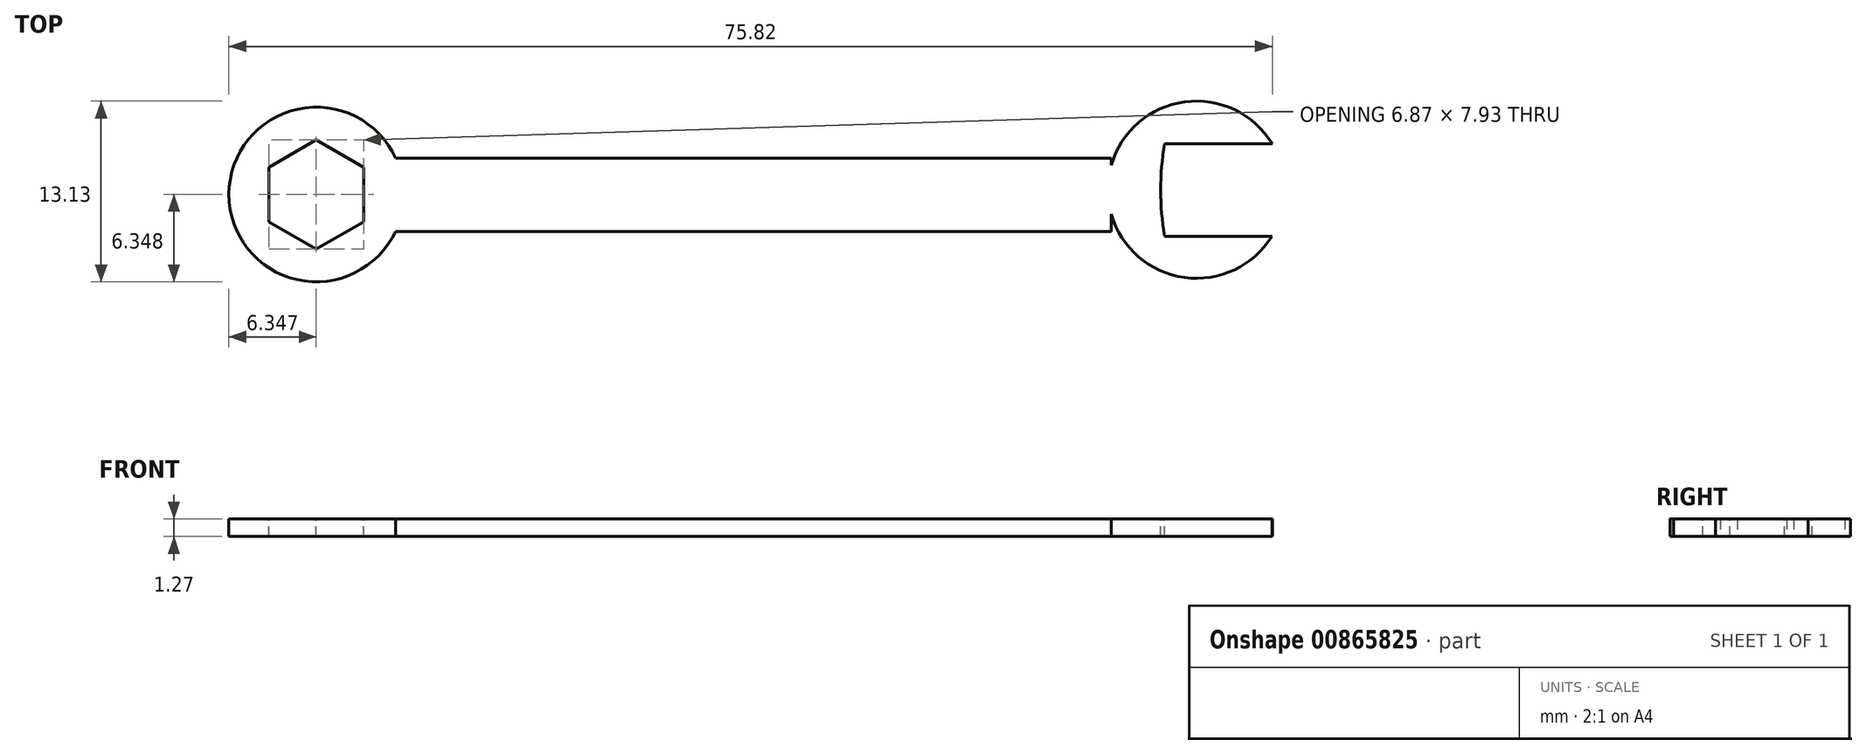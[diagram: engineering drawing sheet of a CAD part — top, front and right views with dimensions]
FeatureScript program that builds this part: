
annotation { "Feature Type Name" : "Feature", "Feature Type Description" : "" }
export const myFeature = defineFeature(function(context is Context, id is Id, definition is map)
    precondition{}
    {
        {
            var Q0;
            Q0=qCreatedBy(makeId("Top.planeOp"),FACE);
            var sketch = newSketch(context, id + "F0", { "sketchPlane" : qUnion([Q0])});
            skCircle(sketch, "E0", {"center": v(-57.77, 15.17) * mm, "radius": 6.35 * mm});
            skSolve(sketch);
        }
        {
            var Q0;
            Q0=makeQuery(id+"F0.imprint","IMPRINT",FACE,{"disambiguationData":[TD([[makeQuery(id+"F0.imprint","IMPRINT",EDGE,{"derivedFrom":sQuery(id+"F0.wireOp",EDGE,"E0")}),1.0]])]});
            extrude(context, id + "F1", {"entities" : qUnion([Q0]), "depth" : 1.27 * mm, "offsetDistance" : 25.4 * mm});
        }
        {
            var Q0;
            Q0=makeQuery(id+"F0.imprint","IMPRINT",FACE,{"disambiguationData":[TD([[makeQuery(id+"F0.imprint","IMPRINT",EDGE,{"derivedFrom":sQuery(id+"F0.wireOp",EDGE,"E0")}),1.0]])]});
            extrude(context, id + "F2", {"entities" : qUnion([Q0]), "operationType" : NewBodyOperationType.ADD, "depth" : 1.27 * mm, "offsetDistance" : 25.4 * mm});
        }
        {
            var Q0;
            Q0=qCreatedBy(makeId("Top.planeOp"),FACE);
            var sketch = newSketch(context, id + "F3", { "sketchPlane" : qUnion([Q0])});
            skLineSegment(sketch, "E1.bottom", {"start": v(-52.79, 12.49) * mm, "end": v(0, 12.49) * mm});
            skLineSegment(sketch, "E1.top", {"start": v(-52.79, 17.8) * mm, "end": v(0, 17.8) * mm});
            skLineSegment(sketch, "E1.left", {"start": v(-52.79, 12.49) * mm, "end": v(-52.79, 17.8) * mm});
            skLineSegment(sketch, "E1.right", {"start": v(0, 12.49) * mm, "end": v(0, 17.8) * mm});
            skSolve(sketch);
        }
        {
            var Q0;
            Q0 = qSketchRegion(id + "F3", true);
            extrude(context, id + "F4", {"entities" : qUnion([Q0]), "operationType" : NewBodyOperationType.ADD, "depth" : 1.27 * mm, "offsetDistance" : 25.4 * mm});
        }
        {
            var Q0;
            Q0=qCreatedBy(makeId("Top.planeOp"),FACE);
            var sketch = newSketch(context, id + "F5", { "sketchPlane" : qUnion([Q0])});
            skCircle(sketch, "E2", {"center": v(6.2, 15.51) * mm, "radius": 6.44 * mm});
            skSolve(sketch);
        }
        {
            var Q0;
            Q0 = qSketchRegion(id + "F5", true);
            extrude(context, id + "F6", {"entities" : qUnion([Q0]), "operationType" : NewBodyOperationType.ADD, "depth" : 1.27 * mm, "offsetDistance" : 25.4 * mm});
        }
        {
            var Q0;
            Q0=makeQuery(id+"F6.boolean.opBoolean","MERGE",FACE,{"derivedFrom":[makeQuery(id+"F4.boolean.opBoolean","MERGE",FACE,{"derivedFrom":[makeQuery(id+"F1.opExtrude","CAP_FACE",FACE,{"disambiguationData":[OSD([sQuery(id+"F0.wireOp",EDGE,"E0")])],"isStart":false}),makeQuery(id+"F4.opExtrude","CAP_FACE",FACE,{"disambiguationData":[OSD([sQuery(id+"F3.wireOp",EDGE,"E1.bottom"),sQuery(id+"F3.wireOp",EDGE,"E1.top"),sQuery(id+"F3.wireOp",EDGE,"E1.left"),sQuery(id+"F3.wireOp",EDGE,"E1.right")])],"isStart":false})]}),makeQuery(id+"F6.opExtrude","CAP_FACE",FACE,{"disambiguationData":[OSD([sQuery(id+"F5.wireOp",EDGE,"E2")])],"isStart":false})]});
            var sketch = newSketch(context, id + "F7", { "sketchPlane" : qUnion([Q0])});
            skCircle(sketch, "E3.cCircle", {"center": v(-57.77, 15.17) * mm, "radius": 3.43 * mm, "construction": true});
            skLineSegment(sketch, "E3.0", {"start": v(-54.34, 17.15) * mm, "end": v(-54.34, 13.19) * mm});
            skLineSegment(sketch, "E3.1", {"start": v(-54.34, 13.19) * mm, "end": v(-57.77, 11.2) * mm});
            skLineSegment(sketch, "E3.2", {"start": v(-57.77, 11.2) * mm, "end": v(-61.2, 13.19) * mm});
            skLineSegment(sketch, "E3.3", {"start": v(-61.2, 13.19) * mm, "end": v(-61.2, 17.15) * mm});
            skLineSegment(sketch, "E3.4", {"start": v(-61.2, 17.15) * mm, "end": v(-57.77, 19.13) * mm});
            skLineSegment(sketch, "E3.5", {"start": v(-57.77, 19.13) * mm, "end": v(-54.34, 17.15) * mm});
            skPoint(sketch, "E3.0.midPoint", {"position": v(-54.34, 15.17) * mm});
            skSolve(sketch);
        }
        {
            var Q0;
            Q0 = qSketchRegion(id + "F7", true);
            extrude(context, id + "F8", {"entities" : qUnion([Q0]), "operationType" : NewBodyOperationType.REMOVE, "oppositeDirection" : true, "depth" : 12.7 * mm, "offsetDistance" : 25.4 * mm, "hasSecondDirection" : true, "secondDirectionOppositeDirection" : false, "secondDirectionDepth" : 25.4 * mm});
        }
        {
            var Q0;
            Q0=makeQuery(id+"F6.boolean.opBoolean","MERGE",FACE,{"derivedFrom":[makeQuery(id+"F4.boolean.opBoolean","MERGE",FACE,{"derivedFrom":[makeQuery(id+"F1.opExtrude","CAP_FACE",FACE,{"disambiguationData":[OSD([sQuery(id+"F0.wireOp",EDGE,"E0")])],"isStart":false}),makeQuery(id+"F4.opExtrude","CAP_FACE",FACE,{"disambiguationData":[OSD([sQuery(id+"F3.wireOp",EDGE,"E1.bottom"),sQuery(id+"F3.wireOp",EDGE,"E1.top"),sQuery(id+"F3.wireOp",EDGE,"E1.left"),sQuery(id+"F3.wireOp",EDGE,"E1.right")])],"isStart":false})]}),makeQuery(id+"F6.opExtrude","CAP_FACE",FACE,{"disambiguationData":[OSD([sQuery(id+"F5.wireOp",EDGE,"E2")])],"isStart":false})]});
            var sketch = newSketch(context, id + "F9", { "sketchPlane" : qUnion([Q0])});
            skLineSegment(sketch, "E4.bottom", {"start": v(11.68, 12.13) * mm, "end": v(3.88, 12.13) * mm});
            skLineSegment(sketch, "E4.top", {"start": v(11.68, 18.85) * mm, "end": v(3.88, 18.85) * mm});
            skArc(sketch, "E5", {"start": v(3.88, 18.85) * mm, "mid": v(3.58, 15.5) * mm, "end": v(3.88, 12.13) * mm});
            skArc(sketch, "E6", {"start": v(11.68, 12.13) * mm, "mid": v(15.03, 15.5) * mm, "end": v(11.68, 18.85) * mm});
            skSolve(sketch);
        }
        {
            var Q0;
            Q0 = qSketchRegion(id + "F9", true);
            extrude(context, id + "F10", {"entities" : qUnion([Q0]), "operationType" : NewBodyOperationType.REMOVE, "oppositeDirection" : true, "depth" : 12.7 * mm, "offsetDistance" : 25.4 * mm});
        }
    });
